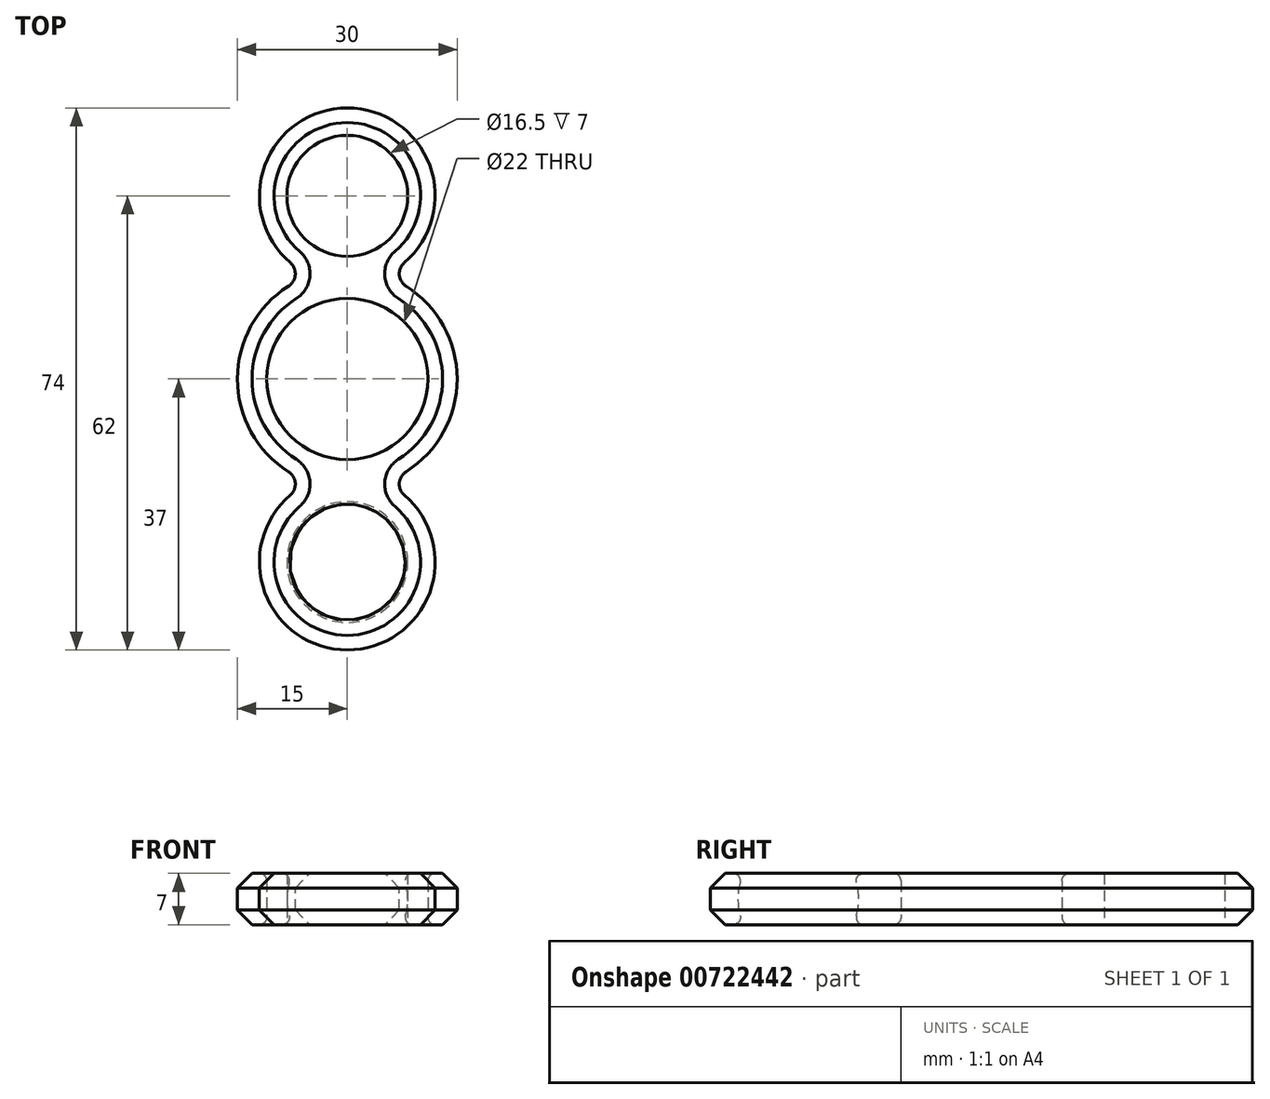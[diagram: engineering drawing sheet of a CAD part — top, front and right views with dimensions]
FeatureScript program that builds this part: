
annotation { "Feature Type Name" : "Feature", "Feature Type Description" : "" }
export const myFeature = defineFeature(function(context is Context, id is Id, definition is map)
    precondition{}
    {
        {
            var Q0;
            Q0=qCreatedBy(makeId("Top.planeOp"),FACE);
            var sketch = newSketch(context, id + "F0", { "sketchPlane" : qUnion([Q0])});
            skLineSegment(sketch, "E0", {"start": v(0, 0) * mm, "end": v(0, 25) * mm, "construction": true});
            skCircle(sketch, "E1", {"center": v(0, 25) * mm, "radius": 8.25 * mm});
            skArc(sketch, "E2", {"start": v(5.06, 14.12) * mm, "mid": v(0, 37) * mm, "end": v(-5.06, 14.12) * mm});
            skCircle(sketch, "E3", {"center": v(0, 0) * mm, "radius": 11 * mm});
            skArc(sketch, "E4", {"start": v(5.06, -14.12) * mm, "mid": v(11.44, -9.7) * mm, "end": v(14.76, -2.68) * mm});
            skArc(sketch, "E5.1.2", {"start": v(-5.06, -14.12) * mm, "mid": v(0, -37) * mm, "end": v(5.06, -14.12) * mm});
            skCircle(sketch, "E5.1.3", {"center": v(0, -25) * mm, "radius": 8.25 * mm});
            skArc(sketch, "E6.trimOffspring", {"start": v(14.76, -2.68) * mm, "mid": v(13, 7.5) * mm, "end": v(5.06, 14.12) * mm});
            skArc(sketch, "E7.trimOffspring", {"start": v(-5.06, 14.12) * mm, "mid": v(-15, 0) * mm, "end": v(-5.06, -14.12) * mm});
            skLineSegment(sketch, "E8", {"start": v(0, 0) * mm, "end": v(0, -25) * mm, "construction": true});
            skLineSegment(sketch, "E9", {"start": v(0, 0) * mm, "end": v(21.65, 12.5) * mm, "construction": true});
            skSolve(sketch);
        }
        {
            var Q0;
            Q0=qSketchRegion(id+"F0",true);
            extrude(context, id + "F1", {"entities" : qUnion([Q0]), "depth" : 7 * mm, "offsetDistance" : 25 * mm});
        }
        {
            var Q0;
            Q0=makeQuery(id+"F1.opExtrude","SWEPT_EDGE",EDGE,{"disambiguationData":[OSD([sQuery(id+"F0.wireOp",EDGE,"E4"),sQuery(id+"F0.wireOp",EDGE,"E5.1.2")])]});
            var Q1;
            Q1=makeQuery(id+"F1.opExtrude","SWEPT_EDGE",EDGE,{"disambiguationData":[OSD([sQuery(id+"F0.wireOp",EDGE,"E4"),sQuery(id+"F0.wireOp",EDGE,"E5.2.2")])]});
            var Q2;
            Q2=makeQuery(id+"F1.opExtrude","SWEPT_EDGE",EDGE,{"disambiguationData":[OSD([sQuery(id+"F0.wireOp",EDGE,"E5.2.2"),sQuery(id+"F0.wireOp",EDGE,"E6.trimOffspring")])]});
            var Q3;
            Q3=makeQuery(id+"F1.opExtrude","SWEPT_EDGE",EDGE,{"disambiguationData":[OSD([sQuery(id+"F0.wireOp",EDGE,"E2"),sQuery(id+"F0.wireOp",EDGE,"E6.trimOffspring")])]});
            var Q4;
            Q4=makeQuery(id+"F1.opExtrude","SWEPT_EDGE",EDGE,{"disambiguationData":[OSD([sQuery(id+"F0.wireOp",EDGE,"E2"),sQuery(id+"F0.wireOp",EDGE,"E7.trimOffspring")])]});
            var Q5;
            Q5=makeQuery(id+"F1.opExtrude","SWEPT_EDGE",EDGE,{"disambiguationData":[OSD([sQuery(id+"F0.wireOp",EDGE,"E5.1.2"),sQuery(id+"F0.wireOp",EDGE,"E7.trimOffspring")])]});
            fillet(context, id + "F2", {"entities" : qUnion([Q0, Q1, Q2, Q3, Q4, Q5]), "radius" : 2 * mm, "tangentPropagation" : true, "allowEdgeOverflow" : false});
        }
        {
            var Q0;
            Q0=makeQuery(id+"F1.opExtrude","CAP_EDGE",EDGE,{"disambiguationData":[OSD([sQuery(id+"F0.wireOp",EDGE,"E5.2.2")])],"isStart":true});
            var Q1;
            Q1=makeQuery(id+"F1.opExtrude","CAP_EDGE",EDGE,{"disambiguationData":[OSD([sQuery(id+"F0.wireOp",EDGE,"E5.2.2")])],"isStart":false});
            var Q2;
            Q2=makeQuery(id+"F1.opExtrude","CAP_EDGE",EDGE,{"disambiguationData":[OSD([sQuery(id+"F0.wireOp",EDGE,"E5.1.2")])],"isStart":false});
            var Q3;
            Q3=makeQuery(id+"F1.opExtrude","CAP_EDGE",EDGE,{"disambiguationData":[OSD([sQuery(id+"F0.wireOp",EDGE,"E5.1.2")])],"isStart":true});
            chamfer(context, id + "F3", {"entities" : qUnion([Q0, Q1, Q2, Q3]), "width" : 2 * mm, "tangentPropagation" : true});
        }
        {
            var Q0;
            Q0=qCreatedBy(makeId("Top.planeOp"),FACE);
            var sketch = newSketch(context, id + "F4", { "sketchPlane" : qUnion([Q0])});
            skCircle(sketch, "E10.0", {"center": v(0, -25) * mm, "radius": 8.25 * mm, "construction": true});
            skLineSegment(sketch, "E11", {"start": v(0, 0) * mm, "end": v(0, -25) * mm, "construction": true});
            skCircle(sketch, "E12.0", {"center": v(0, 25) * mm, "radius": 8.25 * mm, "construction": true});
            skLineSegment(sketch, "E13", {"start": v(0, 0) * mm, "end": v(0, 25) * mm, "construction": true});
            skCircle(sketch, "E14.0", {"center": v(24.25, -14) * mm, "radius": 13 * mm, "construction": true});
            skLineSegment(sketch, "E15", {"start": v(0, 0) * mm, "end": v(24.25, -14) * mm, "construction": true});
            skSolve(sketch);
        }
        {
            var Q0;
            {var subQ0=sQuery(id+"F0.wireOp",EDGE,"E5.1.2");Q0=makeQuery(id+"F3.opChamfer","BLEND_EDGE",EDGE,{"blendedFrom":[makeQuery(id+"F1.opExtrude","CAP_EDGE",EDGE,{"disambiguationData":[OSD([subQ0])],"isStart":false}),makeQuery(id+"F1.opExtrude","CAP_FACE",FACE,{"disambiguationData":[OSD([sQuery(id+"F0.wireOp",EDGE,"E1"),sQuery(id+"F0.wireOp",EDGE,"E2"),sQuery(id+"F0.wireOp",EDGE,"E3"),sQuery(id+"F0.wireOp",EDGE,"E4"),subQ0,sQuery(id+"F0.wireOp",EDGE,"E5.1.3"),sQuery(id+"F0.wireOp",EDGE,"E5.2.2"),sQuery(id+"F0.wireOp",EDGE,"E5.2.3"),sQuery(id+"F0.wireOp",EDGE,"E6.trimOffspring"),sQuery(id+"F0.wireOp",EDGE,"E7.trimOffspring")])],"isStart":false})],"blendedInto":[makeQuery(id+"F1.opExtrude","CAP_FACE",FACE,{"disambiguationData":[OSD([sQuery(id+"F0.wireOp",EDGE,"E1"),sQuery(id+"F0.wireOp",EDGE,"E2"),sQuery(id+"F0.wireOp",EDGE,"E3"),sQuery(id+"F0.wireOp",EDGE,"E4"),subQ0,sQuery(id+"F0.wireOp",EDGE,"E5.1.3"),sQuery(id+"F0.wireOp",EDGE,"E5.2.2"),sQuery(id+"F0.wireOp",EDGE,"E5.2.3"),sQuery(id+"F0.wireOp",EDGE,"E6.trimOffspring"),sQuery(id+"F0.wireOp",EDGE,"E7.trimOffspring")])],"isStart":false})]});}
            cPoint(context, id + "F5", {"entities" : qUnion([Q0]), "parameter" : 0.5});
        }
        {
            var Q0;
            Q0=sQuery(id+"F4.wireOp",VERTEX,"E11.start");
            var Q1;
            Q1=sQuery(id+"F4.wireOp",VERTEX,"E10.0.center");
            var Q2;
            Q2=qCreatedBy(id+"F5",VERTEX);
            cPlane(context, id + "F6", {"entities" : qUnion([Q0, Q1, Q2]), "cplaneType" : CPlaneType.THREE_POINT, "offset" : 25 * mm, "width" : 150 * mm, "height" : 150 * mm});
        }
        {
            var Q0;
            Q0=qCreatedBy(id+"F6.planeOp",FACE);
            var sketch = newSketch(context, id + "F7", { "sketchPlane" : qUnion([Q0])});
            skLineSegment(sketch, "E16.0", {"start": v(-33.25, 7) * mm, "end": v(-32.47, 7) * mm, "construction": true});
            skLineSegment(sketch, "E17.1", {"start": v(-33.25, 0) * mm, "end": v(-32.47, 0) * mm, "construction": true});
            skLineSegment(sketch, "E18", {"start": v(-33.25, 7) * mm, "end": v(-33.25, 0) * mm});
            skLineSegment(sketch, "E19", {"start": v(-25, 0) * mm, "end": v(-25, 7) * mm, "construction": true});
            skArc(sketch, "E20", {"start": v(-32.47, 7) * mm, "mid": v(-33.25, 3.5) * mm, "end": v(-32.47, 0) * mm});
            skLineSegment(sketch, "E21", {"start": v(-33.25, 7) * mm, "end": v(-32.47, 7) * mm});
            skLineSegment(sketch, "E22", {"start": v(-33.25, 0) * mm, "end": v(-32.47, 0) * mm});
            skLineSegment(sketch, "E23.trimOffspring", {"start": v(-25, 7) * mm, "end": v(-16.75, 7) * mm, "construction": true});
            skLineSegment(sketch, "E24.trimOffspring", {"start": v(-25, 0) * mm, "end": v(-16.75, 0) * mm, "construction": true});
            skSolve(sketch);
        }
        {
            var Q0;
            Q0=qSketchRegion(id+"F7",true);
            var Q1;
            Q1=sQuery(id+"F7.wireOp",EDGE,"E19");
            revolve(context, id + "F8", {"operationType" : NewBodyOperationType.ADD, "surfaceOperationType" : NewSurfaceOperationType.NEW, "entities" : qUnion([Q0]), "axis" : qUnion([Q1]), "revolveType" : RevolveType.FULL});
        }
        {
            var Q0;
            Q0=makeQuery(id+"F8.opRevolve","SWEPT_EDGE",EDGE,{"disambiguationData":[OSD([sQuery(id+"F7.wireOp",EDGE,"E20"),sQuery(id+"F7.wireOp",EDGE,"E21")])]});
            var Q1;
            Q1=makeQuery(id+"F8.opRevolve","SWEPT_EDGE",EDGE,{"disambiguationData":[OSD([sQuery(id+"F7.wireOp",EDGE,"E20"),sQuery(id+"F7.wireOp",EDGE,"E22")])]});
            var Q2;
            Q2=makeQuery(id+"Fynh9oEJvHPlE7w_1.2.F8.opRevolve","SWEPT_EDGE",EDGE,{"disambiguationData":[OSD([sQuery(id+"F7.wireOp",EDGE,"E20"),sQuery(id+"F7.wireOp",EDGE,"E21")])]});
            var Q3;
            Q3=makeQuery(id+"Fynh9oEJvHPlE7w_1.2.F8.opRevolve","SWEPT_EDGE",EDGE,{"disambiguationData":[OSD([sQuery(id+"F7.wireOp",EDGE,"E20"),sQuery(id+"F7.wireOp",EDGE,"E22")])]});
            var Q4;
            Q4=makeQuery(id+"Fynh9oEJvHPlE7w_1.1.F8.opRevolve","SWEPT_EDGE",EDGE,{"disambiguationData":[OSD([sQuery(id+"F7.wireOp",EDGE,"E20"),sQuery(id+"F7.wireOp",EDGE,"E21")])]});
            var Q5;
            Q5=makeQuery(id+"Fynh9oEJvHPlE7w_1.1.F8.opRevolve","SWEPT_EDGE",EDGE,{"disambiguationData":[OSD([sQuery(id+"F7.wireOp",EDGE,"E20"),sQuery(id+"F7.wireOp",EDGE,"E22")])]});
            var Q6;
            Q6=makeQuery(id+"F1.opExtrude","CAP_EDGE",EDGE,{"disambiguationData":[OSD([sQuery(id+"F0.wireOp",EDGE,"E3")])],"isStart":true});
            var Q7;
            Q7=makeQuery(id+"F1.opExtrude","CAP_EDGE",EDGE,{"disambiguationData":[OSD([sQuery(id+"F0.wireOp",EDGE,"E3")])],"isStart":false});
            fillet(context, id + "F9", {"entities" : qUnion([Q0, Q1, Q2, Q3, Q4, Q5, Q6, Q7]), "radius" : 1 * mm, "tangentPropagation" : true, "allowEdgeOverflow" : false});
        }
    });
